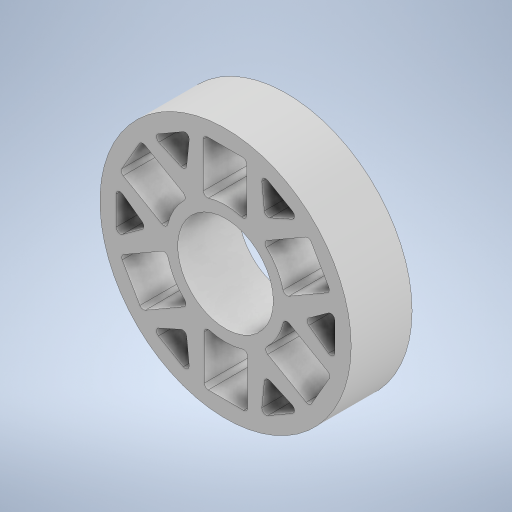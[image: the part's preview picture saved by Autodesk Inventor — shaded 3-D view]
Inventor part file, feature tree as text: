
AUTODESK INVENTOR PART (.ipt)
format: ipt  version: 2024 (Build 280153000, 153)  size: 400,384 bytes
history: native  units: in
note: dims shown in document units (in); Inventor stores cm internally (conversion verified against a paired STEP export)
features: extrude x1, fillet x1, sketch x1
ambient origin geometry x8: Origin, YZ Plane, XZ Plane, XY Plane, X Axis, Y Axis, Z Axis, Center Point
bodies: Body1 (feature_tree)
feature tree (3):
  extrude  "Extrusion2"  Depth=0.065in
  fillet  "Fillet1"  Radius=0.19in
  sketch  "Sketch1"  dims[d0=1.57in d3=4.125in d7=0.19in d35=2.3622in d37=2.3622in d38=0.89in d39=0.71in d40=0.3625in d41=360.0deg d42=0.3625in d43=0.3625in d44=0.3625in d45=0.5in d46=0.5in d49=360.0deg d50=1.0in d51=0.0in d52=0.065in]
